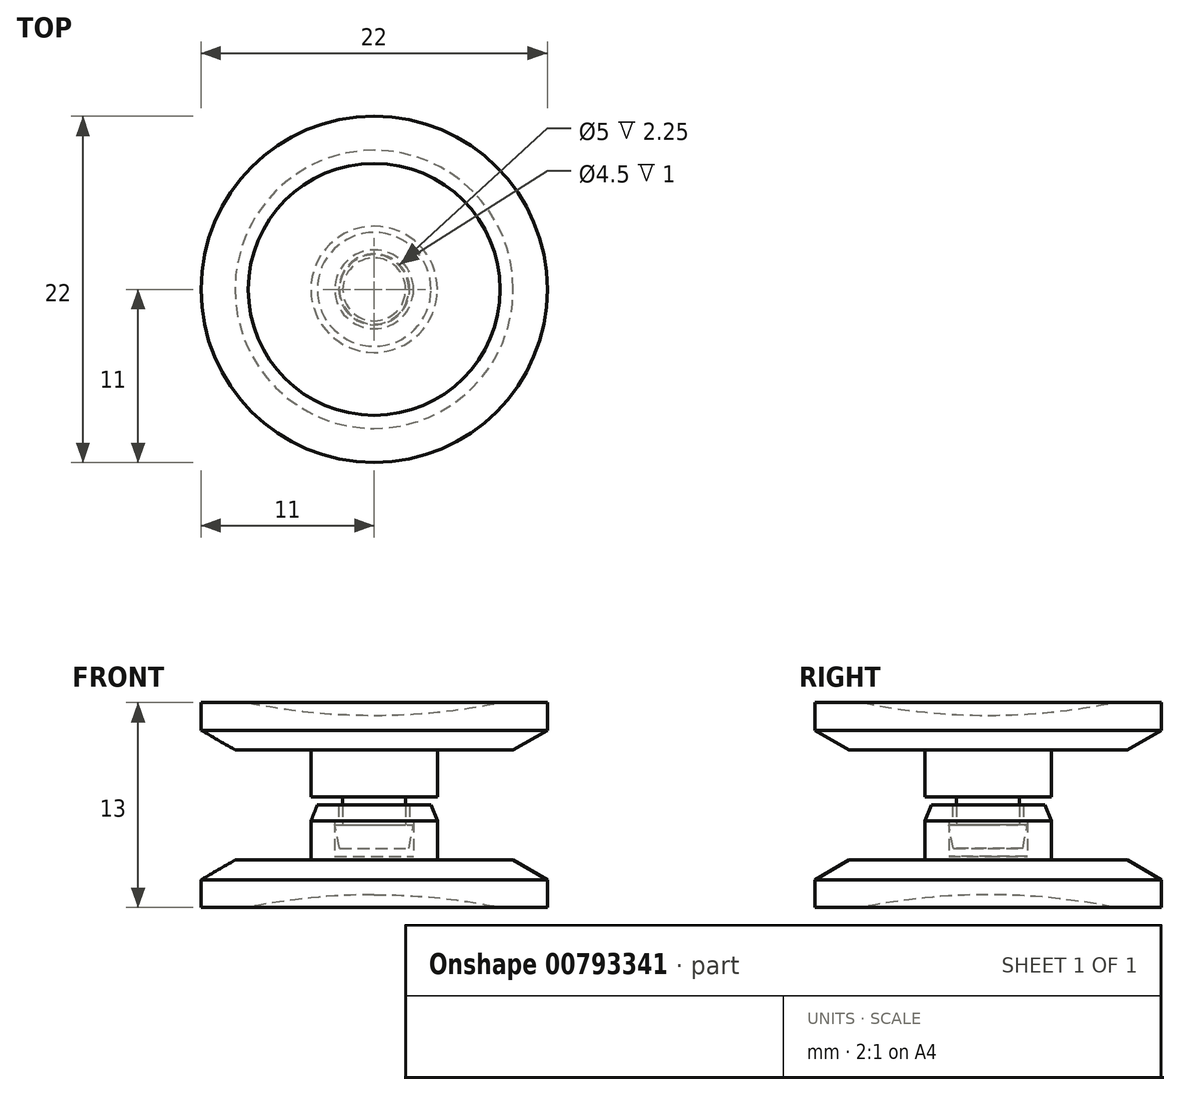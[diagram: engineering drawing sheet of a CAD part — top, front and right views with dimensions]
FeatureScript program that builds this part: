
annotation { "Feature Type Name" : "Feature", "Feature Type Description" : "" }
export const myFeature = defineFeature(function(context is Context, id is Id, definition is map)
    precondition{}
    {
        {
            var Q0;
            Q0=qCreatedBy(makeId("Front.planeOp"),FACE);
            var sketch = newSketch(context, id + "F0", { "sketchPlane" : qUnion([Q0])});
            skLineSegment(sketch, "E0.bottom", {"start": v(9.8, 3.5) * mm, "end": v(-9.8, 3.5) * mm});
            skLineSegment(sketch, "E0.top", {"start": v(9.8, -3.5) * mm, "end": v(-9.8, -3.5) * mm});
            skLineSegment(sketch, "E0.left", {"start": v(11, 2.3) * mm, "end": v(11, -2.3) * mm});
            skLineSegment(sketch, "E0.right", {"start": v(-11, 2.3) * mm, "end": v(-11, -2.3) * mm});
            skPoint(sketch, "E0.middle", {"position": v(0, 0) * mm});
            skPoint(sketch, "E1.visualSharp", {"position": v(11, 3.5) * mm});
            skArc(sketch, "E1.filletArc", {"start": v(11, 2.3) * mm, "mid": v(10.65, 3.15) * mm, "end": v(9.8, 3.5) * mm});
            skPoint(sketch, "E2.visualSharp", {"position": v(-11, 3.5) * mm});
            skArc(sketch, "E2.filletArc", {"start": v(-9.8, 3.5) * mm, "mid": v(-10.65, 3.15) * mm, "end": v(-11, 2.3) * mm});
            skPoint(sketch, "E3.visualSharp", {"position": v(-11, -3.5) * mm});
            skArc(sketch, "E3.filletArc", {"start": v(-11, -2.3) * mm, "mid": v(-10.65, -3.15) * mm, "end": v(-9.8, -3.5) * mm});
            skPoint(sketch, "E4.visualSharp", {"position": v(11, -3.5) * mm});
            skArc(sketch, "E4.filletArc", {"start": v(9.8, -3.5) * mm, "mid": v(10.65, -3.15) * mm, "end": v(11, -2.3) * mm});
            skLineSegment(sketch, "E5", {"start": v(0, 3.5) * mm, "end": v(0, -3.5) * mm, "construction": true});
            skLineSegment(sketch, "E6", {"start": v(-4, 2.3) * mm, "end": v(-4, -2.3) * mm});
            skLineSegment(sketch, "E7", {"start": v(4, -2.3) * mm, "end": v(4, 2.3) * mm});
            skLineSegment(sketch, "E8", {"start": v(-11, 0) * mm, "end": v(-4, 0) * mm, "construction": true});
            skLineSegment(sketch, "E9", {"start": v(-7.5, 0) * mm, "end": v(-7.5, 3.5) * mm, "construction": true});
            skArc(sketch, "E10.MirrorCS", {"start": v(-5.2, 3.5) * mm, "mid": v(-4.35, 3.15) * mm, "end": v(-4, 2.3) * mm});
            skArc(sketch, "E11.MirrorCS", {"start": v(-4, -2.3) * mm, "mid": v(-4.35, -3.15) * mm, "end": v(-5.2, -3.5) * mm});
            skArc(sketch, "E12.MirrorCS", {"start": v(5.2, 3.5) * mm, "mid": v(4.35, 3.15) * mm, "end": v(4, 2.3) * mm});
            skArc(sketch, "E13.MirrorCS", {"start": v(4, -2.3) * mm, "mid": v(4.35, -3.15) * mm, "end": v(5.2, -3.5) * mm});
            skPoint(sketch, "E14.orphan", {"position": v(-4, 3.5) * mm});
            skPoint(sketch, "E15.orphan", {"position": v(-4, -3.5) * mm});
            skSolve(sketch);
        }
        {
            var Q0;
            Q0=qCreatedBy(makeId("Front.planeOp"),FACE);
            var sketch = newSketch(context, id + "F1", { "sketchPlane" : qUnion([Q0])});
            skLineSegment(sketch, "E16", {"start": v(-4.01, 0.5) * mm, "end": v(-4.01, 3.5) * mm});
            skLineSegment(sketch, "E17", {"start": v(-4.01, 3.5) * mm, "end": v(-8.83, 3.5) * mm});
            skLineSegment(sketch, "E18", {"start": v(-11, 4.75) * mm, "end": v(-11, 6.5) * mm});
            skLineSegment(sketch, "E19", {"start": v(-11, 6.5) * mm, "end": v(0, 6.5) * mm, "construction": true});
            skLineSegment(sketch, "E20", {"start": v(0, -2.75) * mm, "end": v(-2.2, -2.75) * mm});
            skLineSegment(sketch, "E21", {"start": v(0, -2.75) * mm, "end": v(0, 5.7) * mm});
            skLineSegment(sketch, "E22", {"start": v(-11, 4.75) * mm, "end": v(-8.83, 3.5) * mm});
            skLineSegment(sketch, "E23", {"start": v(-4.01, 0.5) * mm, "end": v(-2, 0.5) * mm});
            skLineSegment(sketch, "E24", {"start": v(-2, 0.5) * mm, "end": v(-2, -1.25) * mm});
            skLineSegment(sketch, "E25", {"start": v(-2.5, -1.25) * mm, "end": v(-2.2, -2.75) * mm});
            skLineSegment(sketch, "E26", {"start": v(-2, -1.25) * mm, "end": v(-2.5, -1.25) * mm});
            skLineSegment(sketch, "E27", {"start": v(-11, 6.5) * mm, "end": v(-8, 6.5) * mm});
            skArc(sketch, "E28", {"start": v(-8, 6.5) * mm, "mid": v(-4.02, 5.9) * mm, "end": v(0, 5.7) * mm});
            skLineSegment(sketch, "E29", {"start": v(0, 6.5) * mm, "end": v(0, 5.7) * mm, "construction": true});
            skLineSegment(sketch, "E30.0", {"start": v(-11, 0) * mm, "end": v(-4, 0) * mm, "construction": true});
            skSolve(sketch);
        }
        {
            var Q0;
            Q0=qCreatedBy(makeId("Front.planeOp"),FACE);
            var sketch = newSketch(context, id + "F2", { "sketchPlane" : qUnion([Q0])});
            skLineSegment(sketch, "E31", {"start": v(-4.01, -1) * mm, "end": v(-4.01, -3.5) * mm});
            skLineSegment(sketch, "E32", {"start": v(-4.01, -3.5) * mm, "end": v(-8.83, -3.5) * mm});
            skLineSegment(sketch, "E33", {"start": v(-8.83, -3.5) * mm, "end": v(-11, -4.75) * mm});
            skLineSegment(sketch, "E34", {"start": v(-11, -4.75) * mm, "end": v(-11, -6.5) * mm});
            skLineSegment(sketch, "E35", {"start": v(-11, -6.5) * mm, "end": v(0, -6.5) * mm, "construction": true});
            skLineSegment(sketch, "E36", {"start": v(0, -5.7) * mm, "end": v(0, -3.25) * mm});
            skLineSegment(sketch, "E37.0", {"start": v(-11, 0) * mm, "end": v(-4, 0) * mm, "construction": true});
            skPoint(sketch, "E38.0", {"position": v(-2.5, -1.25) * mm});
            skLineSegment(sketch, "E39", {"start": v(-2.5, -1) * mm, "end": v(-2.5, -3.25) * mm});
            skLineSegment(sketch, "E40", {"start": v(-4.01, 0) * mm, "end": v(-4, 0) * mm});
            skLineSegment(sketch, "E41", {"start": v(-2.5, -3.25) * mm, "end": v(0, -3.25) * mm});
            skLineSegment(sketch, "E42", {"start": v(-2.25, -1) * mm, "end": v(-2.25, 0) * mm});
            skLineSegment(sketch, "E43", {"start": v(-2.5, -1) * mm, "end": v(-2.25, -1) * mm});
            skLineSegment(sketch, "E44", {"start": v(-11, -6.5) * mm, "end": v(-8, -6.5) * mm});
            skArc(sketch, "E45", {"start": v(0, -5.7) * mm, "mid": v(-4.02, -5.9) * mm, "end": v(-8, -6.5) * mm});
            skLineSegment(sketch, "E46", {"start": v(-4.01, -1) * mm, "end": v(-3.61, 0) * mm});
            skLineSegment(sketch, "E47.trimOffspring", {"start": v(-3.61, 0) * mm, "end": v(-2.25, 0) * mm});
            skLineSegment(sketch, "E48.0", {"start": v(0, 3.5) * mm, "end": v(0, -3.5) * mm, "construction": true});
            skSolve(sketch);
        }
        {
            var Q0;
            Q0 = qSketchRegion(id + "F1", true);
            var Q1;
            Q1=sQuery(id+"F1.wireOp",EDGE,"E21");
            revolve(context, id + "F3", {"surfaceOperationType" : NewSurfaceOperationType.NEW, "entities" : qUnion([Q0]), "axis" : qUnion([Q1]), "revolveType" : RevolveType.FULL});
        }
        {
            var Q0;
            Q0 = qSketchRegion(id + "F2", true);
            var Q1;
            Q1=sQuery(id+"F2.wireOp",EDGE,"E36");
            revolve(context, id + "F4", {"surfaceOperationType" : NewSurfaceOperationType.NEW, "entities" : qUnion([Q0]), "axis" : qUnion([Q1]), "revolveType" : RevolveType.FULL});
        }
    });
